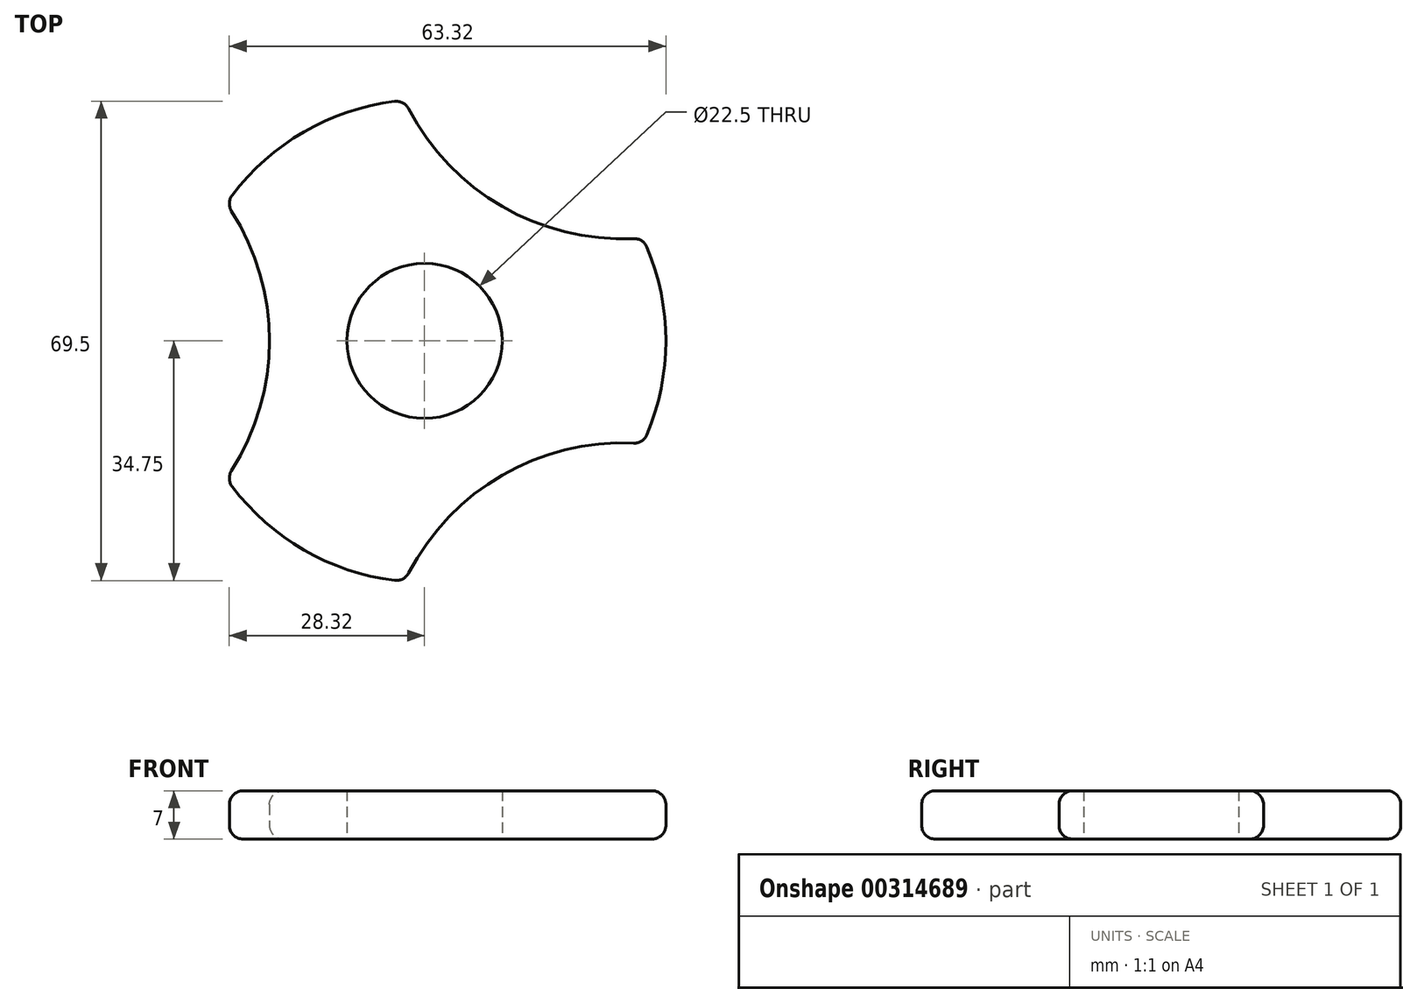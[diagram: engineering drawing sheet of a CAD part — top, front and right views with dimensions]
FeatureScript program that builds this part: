
annotation { "Feature Type Name" : "Feature", "Feature Type Description" : "" }
export const myFeature = defineFeature(function(context is Context, id is Id, definition is map)
    precondition{}
    {
        {
            var Q0;
            Q0=qCreatedBy(makeId("Top.planeOp"),FACE);
            var sketch = newSketch(context, id + "F0", { "sketchPlane" : qUnion([Q0])});
            skCircle(sketch, "E0", {"center": v(0, 0) * mm, "radius": 11.25 * mm});
            skCircle(sketch, "E1", {"center": v(0, 0) * mm, "radius": 35 * mm});
            skCircle(sketch, "E2", {"center": v(-57.5, 0) * mm, "radius": 35 * mm});
            skCircle(sketch, "E3.1.0", {"center": v(28.75, -49.8) * mm, "radius": 35 * mm});
            skCircle(sketch, "E3.2.0", {"center": v(28.75, 49.8) * mm, "radius": 35 * mm});
            skSolve(sketch);
        }
        {
            var Q0;
            Q0=makeQuery(id+"F0.imprint","IMPRINT",FACE,{"disambiguationData":[TD([[makeQuery(id+"F0.imprint","IMPRINT",EDGE,{"derivedFrom":sQuery(id+"F0.wireOp",EDGE,"E0")}),-1.0]])]});
            extrude(context, id + "F1", {"entities" : qUnion([Q0]), "depth" : 7 * mm, "offsetDistance" : 25 * mm});
        }
        {
            var Q0;
            Q0=makeQuery(id+"F1.opExtrude","CAP_EDGE",EDGE,{"disambiguationData":[OSD([sQuery(id+"F0.wireOp",EDGE,"E2")])],"isStart":false});
            var Q1;
            {var subQ0=sQuery(id+"F0.wireOp",EDGE,"E1");Q1=makeQuery(id+"F1.opExtrude","CAP_EDGE",EDGE,{"disambiguationData":[OSD([subQ0]),TDD([makeQuery(id+"F0.imprint","IMPRINT",EDGE,{"disambiguationData":[TD([[makeQuery(id+"F0.imprint","INTERSECT",VERTEX,{"disambiguationData":[OD(0.0)],"derivedFrom":[subQ0,sQuery(id+"F0.wireOp",EDGE,"E3.2.0")]}),-1.0]])],"derivedFrom":subQ0})])],"isStart":false});}
            var Q2;
            Q2=makeQuery(id+"F1.opExtrude","CAP_EDGE",EDGE,{"disambiguationData":[OSD([sQuery(id+"F0.wireOp",EDGE,"E3.2.0")])],"isStart":false});
            var Q3;
            {var subQ0=sQuery(id+"F0.wireOp",EDGE,"E1");Q3=makeQuery(id+"F1.opExtrude","CAP_EDGE",EDGE,{"disambiguationData":[OSD([subQ0]),TDD([makeQuery(id+"F0.imprint","IMPRINT",EDGE,{"disambiguationData":[TD([[makeQuery(id+"F0.imprint","INTERSECT",VERTEX,{"disambiguationData":[OD(1.0)],"derivedFrom":[subQ0,sQuery(id+"F0.wireOp",EDGE,"E3.2.0")]}),1.0]])],"derivedFrom":subQ0})])],"isStart":false});}
            var Q4;
            Q4=makeQuery(id+"F1.opExtrude","CAP_EDGE",EDGE,{"disambiguationData":[OSD([sQuery(id+"F0.wireOp",EDGE,"E3.1.0")])],"isStart":false});
            var Q5;
            {var subQ0=sQuery(id+"F0.wireOp",EDGE,"E1");Q5=makeQuery(id+"F1.opExtrude","CAP_EDGE",EDGE,{"disambiguationData":[OSD([subQ0]),TDD([makeQuery(id+"F0.imprint","IMPRINT",EDGE,{"disambiguationData":[TD([[makeQuery(id+"F0.imprint","INTERSECT",VERTEX,{"disambiguationData":[OD(1.0)],"derivedFrom":[subQ0,sQuery(id+"F0.wireOp",EDGE,"E2")]}),-1.0]])],"derivedFrom":subQ0})])],"isStart":false});}
            var Q6;
            Q6=makeQuery(id+"F1.opExtrude","CAP_EDGE",EDGE,{"disambiguationData":[OSD([sQuery(id+"F0.wireOp",EDGE,"E2")])],"isStart":true});
            var Q7;
            {var subQ0=sQuery(id+"F0.wireOp",EDGE,"E1");Q7=makeQuery(id+"F1.opExtrude","CAP_EDGE",EDGE,{"disambiguationData":[OSD([subQ0]),TDD([makeQuery(id+"F0.imprint","IMPRINT",EDGE,{"disambiguationData":[TD([[makeQuery(id+"F0.imprint","INTERSECT",VERTEX,{"disambiguationData":[OD(0.0)],"derivedFrom":[subQ0,sQuery(id+"F0.wireOp",EDGE,"E3.2.0")]}),-1.0]])],"derivedFrom":subQ0})])],"isStart":true});}
            var Q8;
            {var subQ0=sQuery(id+"F0.wireOp",EDGE,"E1");Q8=makeQuery(id+"F1.opExtrude","CAP_EDGE",EDGE,{"disambiguationData":[OSD([subQ0]),TDD([makeQuery(id+"F0.imprint","IMPRINT",EDGE,{"disambiguationData":[TD([[makeQuery(id+"F0.imprint","INTERSECT",VERTEX,{"disambiguationData":[OD(1.0)],"derivedFrom":[subQ0,sQuery(id+"F0.wireOp",EDGE,"E2")]}),-1.0]])],"derivedFrom":subQ0})])],"isStart":true});}
            var Q9;
            Q9=makeQuery(id+"F1.opExtrude","CAP_EDGE",EDGE,{"disambiguationData":[OSD([sQuery(id+"F0.wireOp",EDGE,"E3.1.0")])],"isStart":true});
            var Q10;
            {var subQ0=sQuery(id+"F0.wireOp",EDGE,"E1");Q10=makeQuery(id+"F1.opExtrude","CAP_EDGE",EDGE,{"disambiguationData":[OSD([subQ0]),TDD([makeQuery(id+"F0.imprint","IMPRINT",EDGE,{"disambiguationData":[TD([[makeQuery(id+"F0.imprint","INTERSECT",VERTEX,{"disambiguationData":[OD(1.0)],"derivedFrom":[subQ0,sQuery(id+"F0.wireOp",EDGE,"E3.2.0")]}),1.0]])],"derivedFrom":subQ0})])],"isStart":true});}
            var Q11;
            Q11=makeQuery(id+"F1.opExtrude","CAP_EDGE",EDGE,{"disambiguationData":[OSD([sQuery(id+"F0.wireOp",EDGE,"E3.2.0")])],"isStart":true});
            var Q12;
            {var subQ0=sQuery(id+"F0.wireOp",EDGE,"E3.2.0");var subQ1=sQuery(id+"F0.wireOp",EDGE,"E1");Q12=makeQuery(id+"F1.opExtrude","SWEPT_EDGE",EDGE,{"disambiguationData":[OSD([subQ1,subQ0]),TDD([makeQuery(id+"F0.imprint","INTERSECT",VERTEX,{"disambiguationData":[OD(1.0)],"derivedFrom":[subQ1,subQ0]})])]});}
            var Q13;
            {var subQ0=sQuery(id+"F0.wireOp",EDGE,"E3.1.0");var subQ1=sQuery(id+"F0.wireOp",EDGE,"E1");Q13=makeQuery(id+"F1.opExtrude","SWEPT_EDGE",EDGE,{"disambiguationData":[OSD([subQ1,subQ0]),TDD([makeQuery(id+"F0.imprint","INTERSECT",VERTEX,{"disambiguationData":[OD(1.0)],"derivedFrom":[subQ1,subQ0]})])]});}
            var Q14;
            {var subQ0=sQuery(id+"F0.wireOp",EDGE,"E3.1.0");var subQ1=sQuery(id+"F0.wireOp",EDGE,"E1");Q14=makeQuery(id+"F1.opExtrude","SWEPT_EDGE",EDGE,{"disambiguationData":[OSD([subQ1,subQ0]),TDD([makeQuery(id+"F0.imprint","INTERSECT",VERTEX,{"disambiguationData":[OD(0.0)],"derivedFrom":[subQ1,subQ0]})])]});}
            var Q15;
            {var subQ0=sQuery(id+"F0.wireOp",EDGE,"E2");var subQ1=sQuery(id+"F0.wireOp",EDGE,"E1");Q15=makeQuery(id+"F1.opExtrude","SWEPT_EDGE",EDGE,{"disambiguationData":[OSD([subQ1,subQ0]),TDD([makeQuery(id+"F0.imprint","INTERSECT",VERTEX,{"disambiguationData":[OD(1.0)],"derivedFrom":[subQ1,subQ0]})])]});}
            var Q16;
            {var subQ0=sQuery(id+"F0.wireOp",EDGE,"E2");var subQ1=sQuery(id+"F0.wireOp",EDGE,"E1");Q16=makeQuery(id+"F1.opExtrude","SWEPT_EDGE",EDGE,{"disambiguationData":[OSD([subQ1,subQ0]),TDD([makeQuery(id+"F0.imprint","INTERSECT",VERTEX,{"disambiguationData":[OD(0.0)],"derivedFrom":[subQ1,subQ0]})])]});}
            var Q17;
            {var subQ0=sQuery(id+"F0.wireOp",EDGE,"E3.2.0");var subQ1=sQuery(id+"F0.wireOp",EDGE,"E1");Q17=makeQuery(id+"F1.opExtrude","SWEPT_EDGE",EDGE,{"disambiguationData":[OSD([subQ1,subQ0]),TDD([makeQuery(id+"F0.imprint","INTERSECT",VERTEX,{"disambiguationData":[OD(0.0)],"derivedFrom":[subQ1,subQ0]})])]});}
            fillet(context, id + "F2", {"entities" : qUnion([Q0, Q1, Q2, Q3, Q4, Q5, Q6, Q7, Q8, Q9, Q10, Q11, Q12, Q13, Q14, Q15, Q16, Q17]), "radius" : 2 * mm, "tangentPropagation" : true, "allowEdgeOverflow" : false});
        }
    });
